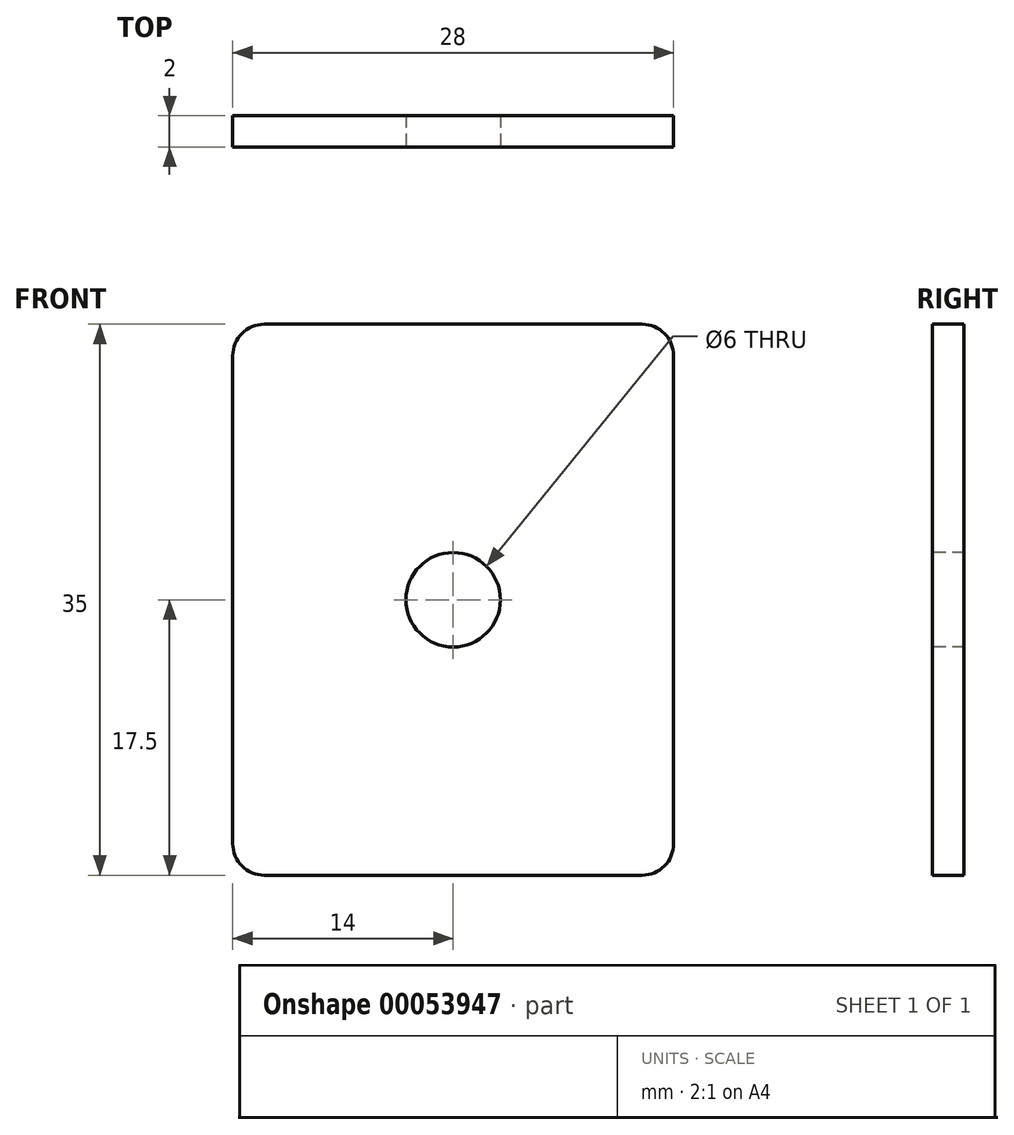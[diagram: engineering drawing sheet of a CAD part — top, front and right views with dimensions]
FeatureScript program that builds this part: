
annotation { "Feature Type Name" : "Feature", "Feature Type Description" : "" }
export const myFeature = defineFeature(function(context is Context, id is Id, definition is map)
    precondition{}
    {
        {
            var Q0;
            Q0=qCreatedBy(makeId("Top.planeOp"),FACE);
            var sketch = newSketch(context, id + "F0", { "sketchPlane" : qUnion([Q0])});
            skLineSegment(sketch, "E0.rect.bottom", {"start": v(12, -17.5) * mm, "end": v(-12, -17.5) * mm});
            skLineSegment(sketch, "E0.rect.top", {"start": v(12, 17.5) * mm, "end": v(-12, 17.5) * mm});
            skLineSegment(sketch, "E0.rect.left", {"start": v(14, -15.5) * mm, "end": v(14, 15.5) * mm});
            skLineSegment(sketch, "E0.rect.right", {"start": v(-14, -15.5) * mm, "end": v(-14, 15.5) * mm});
            skPoint(sketch, "E0.rect.middle", {"position": v(0, 0) * mm});
            skPoint(sketch, "E1.visualSharp", {"position": v(-14, 17.5) * mm});
            skArc(sketch, "E1.filletArc", {"start": v(-12, 17.5) * mm, "mid": v(-13.41, 16.91) * mm, "end": v(-14, 15.5) * mm});
            skPoint(sketch, "E2.visualSharp", {"position": v(14, 17.5) * mm});
            skArc(sketch, "E2.filletArc", {"start": v(14, 15.5) * mm, "mid": v(13.41, 16.91) * mm, "end": v(12, 17.5) * mm});
            skPoint(sketch, "E3.visualSharp", {"position": v(14, -17.5) * mm});
            skArc(sketch, "E3.filletArc", {"start": v(12, -17.5) * mm, "mid": v(13.41, -16.91) * mm, "end": v(14, -15.5) * mm});
            skPoint(sketch, "E4.visualSharp", {"position": v(-14, -17.5) * mm});
            skArc(sketch, "E4.filletArc", {"start": v(-14, -15.5) * mm, "mid": v(-13.41, -16.91) * mm, "end": v(-12, -17.5) * mm});
            skCircle(sketch, "E5", {"center": v(0, 0) * mm, "radius": 3 * mm});
            skSolve(sketch);
        }
        {
            var Q0;
            Q0=makeQuery(id+"F0.imprint","IMPRINT",FACE,{"disambiguationData":[TD([[makeQuery(id+"F0.imprint","IMPRINT",EDGE,{"derivedFrom":sQuery(id+"F0.wireOp",EDGE,"E0.rect.bottom")}),-1.0]])]});
            extrude(context, id + "F1", {"entities" : qUnion([Q0]), "depth" : 2 * mm});
        }
        {
            var Q0;
            Q0=makeQuery(id+"F1.opExtrude","SWEPT_BODY",BODY,{"disambiguationData":[OSD([sQuery(id+"F0.wireOp",EDGE,"E0.rect.bottom"),sQuery(id+"F0.wireOp",EDGE,"E0.rect.top"),sQuery(id+"F0.wireOp",EDGE,"E0.rect.left"),sQuery(id+"F0.wireOp",EDGE,"E0.rect.right"),sQuery(id+"F0.wireOp",EDGE,"E1.filletArc"),sQuery(id+"F0.wireOp",EDGE,"E2.filletArc"),sQuery(id+"F0.wireOp",EDGE,"E3.filletArc"),sQuery(id+"F0.wireOp",EDGE,"E4.filletArc"),sQuery(id+"F0.wireOp",EDGE,"E5")])]});
            var Q1;
            Q1=makeQuery(id+"F1.opExtrude","CAP_EDGE",EDGE,{"disambiguationData":[OSD([sQuery(id+"F0.wireOp",EDGE,"E0.rect.top")])],"isStart":false});
            transform(context, id + "F2", {"entities" : qUnion([Q0]), "transformType" : TransformType.ROTATION, "transformAxis" : qUnion([Q1]), "angle" : 90 * degree, "makeCopy" : false});
        }
    });
